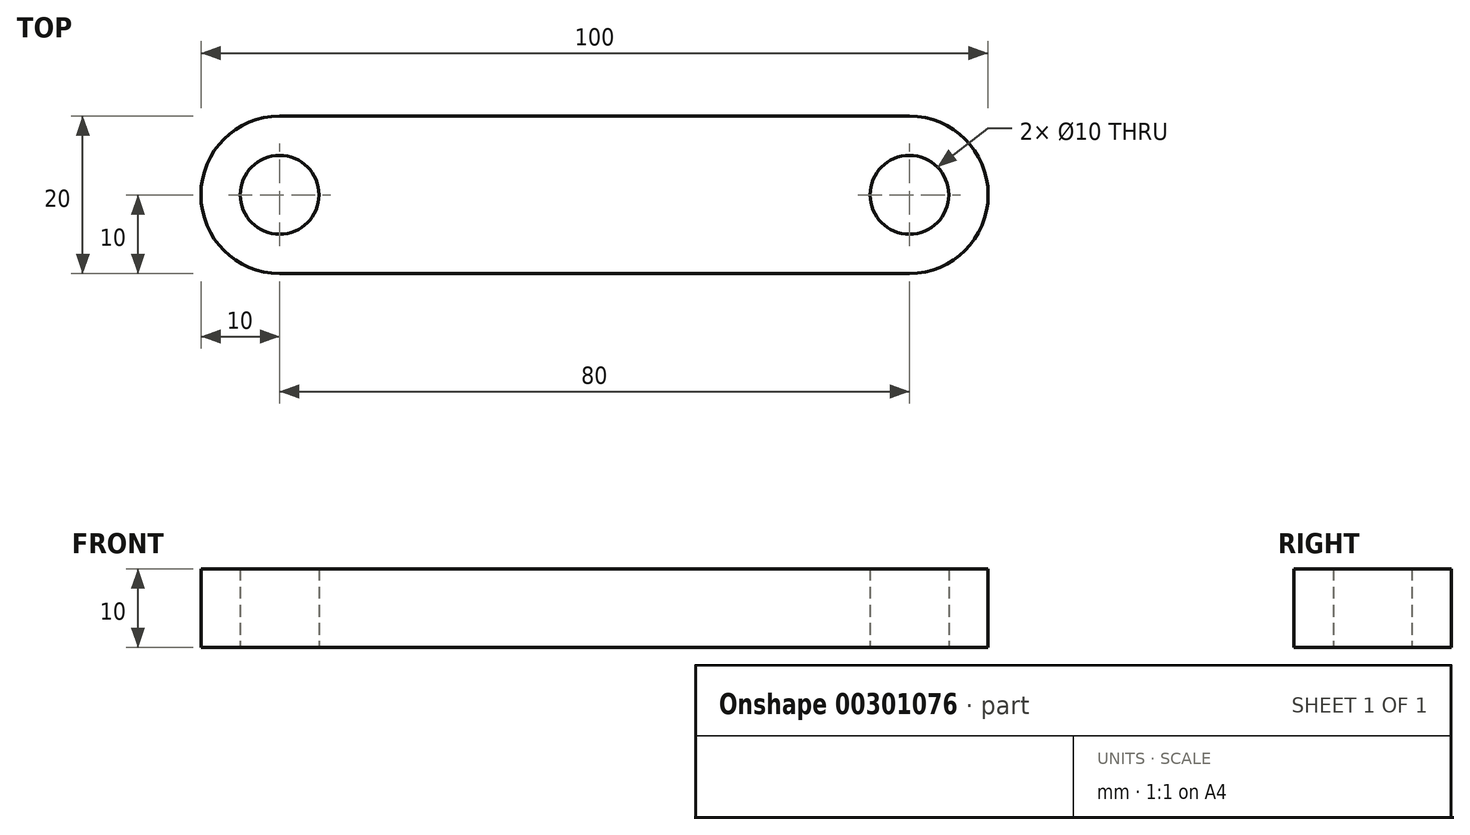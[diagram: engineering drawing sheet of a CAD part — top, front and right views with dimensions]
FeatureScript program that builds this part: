
annotation { "Feature Type Name" : "Feature", "Feature Type Description" : "" }
export const myFeature = defineFeature(function(context is Context, id is Id, definition is map)
    precondition{}
    {
        {
            var Q0;
            Q0=qCreatedBy(makeId("Top.planeOp"),FACE);
            var sketch = newSketch(context, id + "F0", { "sketchPlane" : qUnion([Q0])});
            skLineSegment(sketch, "E0", {"start": v(0, 20) * mm, "end": v(80, 20) * mm});
            skLineSegment(sketch, "E1", {"start": v(0, 0) * mm, "end": v(80, 0) * mm});
            skCircle(sketch, "E2", {"center": v(0, 10) * mm, "radius": 5 * mm});
            skCircle(sketch, "E3", {"center": v(80, 10) * mm, "radius": 5 * mm});
            skArc(sketch, "E4", {"start": v(0, 20) * mm, "mid": v(-10, 10) * mm, "end": v(0, 0) * mm});
            skArc(sketch, "E5", {"start": v(80, 0) * mm, "mid": v(90, 10) * mm, "end": v(80, 20) * mm});
            skSolve(sketch);
        }
        {
            var Q0;
            Q0 = qSketchRegion(id + "F0", true);
            extrude(context, id + "F1", {"entities" : qUnion([Q0]), "depth" : 10 * mm});
        }
    });
